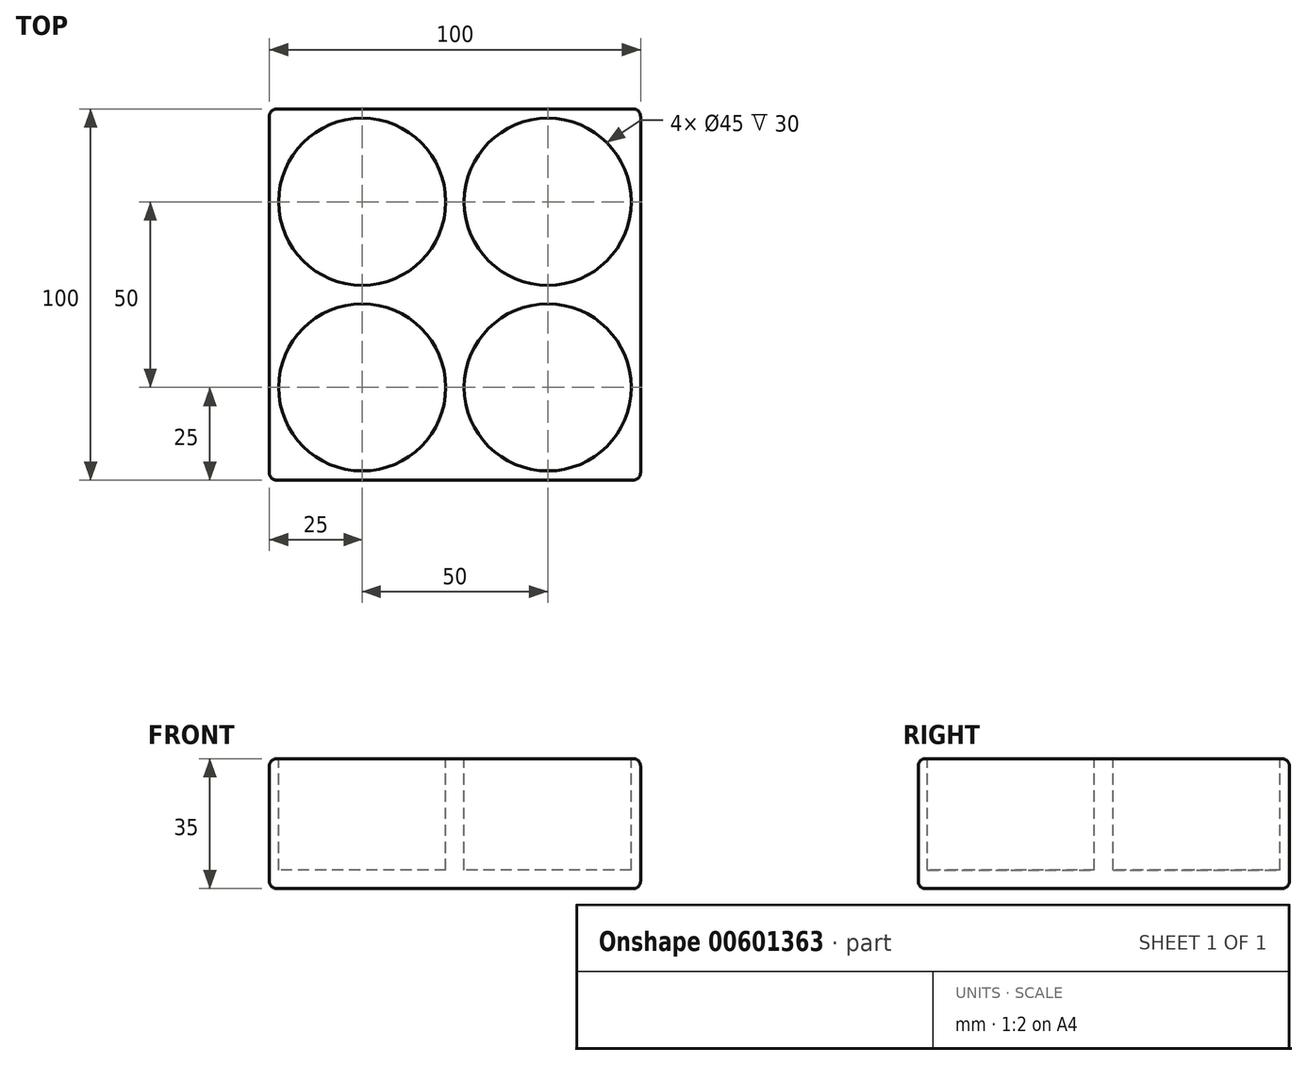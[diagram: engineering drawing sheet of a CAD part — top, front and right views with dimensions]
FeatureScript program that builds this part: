
annotation { "Feature Type Name" : "Feature", "Feature Type Description" : "" }
export const myFeature = defineFeature(function(context is Context, id is Id, definition is map)
    precondition{}
    {
        {
            var Q0;
            Q0=qCreatedBy(makeId("Top.planeOp"),FACE);
            var sketch = newSketch(context, id + "F0", { "sketchPlane" : qUnion([Q0])});
            skLineSegment(sketch, "E0.bottom", {"start": v(50, -50) * mm, "end": v(-50, -50) * mm});
            skLineSegment(sketch, "E0.top", {"start": v(50, 50) * mm, "end": v(-50, 50) * mm});
            skLineSegment(sketch, "E0.left", {"start": v(50, -50) * mm, "end": v(50, 50) * mm});
            skLineSegment(sketch, "E0.right", {"start": v(-50, -50) * mm, "end": v(-50, 50) * mm});
            skPoint(sketch, "E0.middle", {"position": v(0, 0) * mm});
            skPoint(sketch, "E1", {"position": v(-25, 25) * mm});
            skLineSegment(sketch, "E2", {"start": v(-50, 0) * mm, "end": v(50, 0) * mm});
            skLineSegment(sketch, "E3", {"start": v(0, 50) * mm, "end": v(0, 0) * mm});
            skLineSegment(sketch, "E4", {"start": v(-50, 50) * mm, "end": v(0, 0) * mm});
            skLineSegment(sketch, "E5", {"start": v(50, 50) * mm, "end": v(0, 0) * mm});
            skPoint(sketch, "E6", {"position": v(25, 25) * mm});
            skLineSegment(sketch, "E7", {"start": v(-50, -50) * mm, "end": v(0, 0) * mm});
            skPoint(sketch, "E8", {"position": v(-25, -25) * mm});
            skLineSegment(sketch, "E9", {"start": v(0, 0) * mm, "end": v(50, -50) * mm});
            skPoint(sketch, "E10", {"position": v(25, -25) * mm});
            skSolve(sketch);
        }
        {
            var Q0;
            Q0 = qSketchRegion(id + "F0", true);
            extrude(context, id + "F1", {"entities" : qUnion([Q0]), "depth" : 35 * mm, "offsetDistance" : 25 * mm});
        }
        {
            var Q0;
            Q0=makeQuery(id+"F1.opExtrude","CAP_FACE",FACE,{"disambiguationData":[OSD([sQuery(id+"F0.wireOp",EDGE,"E0.bottom"),sQuery(id+"F0.wireOp",EDGE,"E0.top"),sQuery(id+"F0.wireOp",EDGE,"E0.left"),sQuery(id+"F0.wireOp",EDGE,"E0.right")])],"isStart":false});
            var sketch = newSketch(context, id + "F2", { "sketchPlane" : qUnion([Q0])});
            skLineSegment(sketch, "E11", {"start": v(-50, 50) * mm, "end": v(0, 0) * mm});
            skPoint(sketch, "E12", {"position": v(-25, 25) * mm});
            skLineSegment(sketch, "E13", {"start": v(50, 50) * mm, "end": v(0, 0) * mm});
            skPoint(sketch, "E14", {"position": v(25, 25) * mm});
            skLineSegment(sketch, "E15", {"start": v(-50, -50) * mm, "end": v(0, 0) * mm});
            skPoint(sketch, "E16", {"position": v(-25, -25) * mm});
            skLineSegment(sketch, "E17", {"start": v(50, -50) * mm, "end": v(0, 0) * mm});
            skPoint(sketch, "E18", {"position": v(25, -25) * mm});
            skCircle(sketch, "E19", {"center": v(-25, 25) * mm, "radius": 22.5 * mm});
            skCircle(sketch, "E20", {"center": v(25, 25) * mm, "radius": 22.5 * mm});
            skCircle(sketch, "E21", {"center": v(-25, -25) * mm, "radius": 22.5 * mm});
            skCircle(sketch, "E22", {"center": v(25, -25) * mm, "radius": 22.5 * mm});
            skSolve(sketch);
        }
        {
            var Q0;
            {var subQ0=sQuery(id+"F2.wireOp",EDGE,"E19");var subQ1=sQuery(id+"F2.wireOp",EDGE,"E11");var subQ2=makeQuery(id+"F2.imprint","INTERSECT",VERTEX,{"disambiguationData":[OD(0.0)],"derivedFrom":[subQ1,subQ0]});Q0=makeQuery(id+"F2.imprint","IMPRINT",FACE,{"disambiguationData":[TD([[makeQuery(id+"F2.imprint","IMPRINT",EDGE,{"disambiguationData":[TD([[subQ2,-1.0]])],"derivedFrom":subQ1}),1.0]])]});}
            var Q1;
            {var subQ0=sQuery(id+"F2.wireOp",EDGE,"E19");var subQ1=sQuery(id+"F2.wireOp",EDGE,"E11");var subQ2=makeQuery(id+"F2.imprint","INTERSECT",VERTEX,{"disambiguationData":[OD(0.0)],"derivedFrom":[subQ1,subQ0]});Q1=makeQuery(id+"F2.imprint","IMPRINT",FACE,{"disambiguationData":[TD([[makeQuery(id+"F2.imprint","IMPRINT",EDGE,{"disambiguationData":[TD([[subQ2,-1.0]])],"derivedFrom":subQ1}),-1.0]])]});}
            var Q2;
            {var subQ0=sQuery(id+"F2.wireOp",EDGE,"E20");var subQ1=sQuery(id+"F2.wireOp",EDGE,"E13");var subQ2=makeQuery(id+"F2.imprint","INTERSECT",VERTEX,{"disambiguationData":[OD(0.0)],"derivedFrom":[subQ1,subQ0]});Q2=makeQuery(id+"F2.imprint","IMPRINT",FACE,{"disambiguationData":[TD([[makeQuery(id+"F2.imprint","IMPRINT",EDGE,{"disambiguationData":[TD([[subQ2,-1.0]])],"derivedFrom":subQ1}),-1.0]])]});}
            var Q3;
            {var subQ0=sQuery(id+"F2.wireOp",EDGE,"E20");var subQ1=sQuery(id+"F2.wireOp",EDGE,"E13");var subQ2=makeQuery(id+"F2.imprint","INTERSECT",VERTEX,{"disambiguationData":[OD(0.0)],"derivedFrom":[subQ1,subQ0]});Q3=makeQuery(id+"F2.imprint","IMPRINT",FACE,{"disambiguationData":[TD([[makeQuery(id+"F2.imprint","IMPRINT",EDGE,{"disambiguationData":[TD([[subQ2,-1.0]])],"derivedFrom":subQ1}),1.0]])]});}
            var Q4;
            {var subQ0=sQuery(id+"F2.wireOp",EDGE,"E22");var subQ1=sQuery(id+"F2.wireOp",EDGE,"E17");var subQ2=makeQuery(id+"F2.imprint","INTERSECT",VERTEX,{"disambiguationData":[OD(0.0)],"derivedFrom":[subQ1,subQ0]});Q4=makeQuery(id+"F2.imprint","IMPRINT",FACE,{"disambiguationData":[TD([[makeQuery(id+"F2.imprint","IMPRINT",EDGE,{"disambiguationData":[TD([[subQ2,-1.0]])],"derivedFrom":subQ1}),-1.0]])]});}
            var Q5;
            {var subQ0=sQuery(id+"F2.wireOp",EDGE,"E22");var subQ1=sQuery(id+"F2.wireOp",EDGE,"E17");var subQ2=makeQuery(id+"F2.imprint","INTERSECT",VERTEX,{"disambiguationData":[OD(0.0)],"derivedFrom":[subQ1,subQ0]});Q5=makeQuery(id+"F2.imprint","IMPRINT",FACE,{"disambiguationData":[TD([[makeQuery(id+"F2.imprint","IMPRINT",EDGE,{"disambiguationData":[TD([[subQ2,-1.0]])],"derivedFrom":subQ1}),1.0]])]});}
            var Q6;
            {var subQ0=sQuery(id+"F2.wireOp",EDGE,"E21");var subQ1=sQuery(id+"F2.wireOp",EDGE,"E15");var subQ2=makeQuery(id+"F2.imprint","INTERSECT",VERTEX,{"disambiguationData":[OD(0.0)],"derivedFrom":[subQ1,subQ0]});Q6=makeQuery(id+"F2.imprint","IMPRINT",FACE,{"disambiguationData":[TD([[makeQuery(id+"F2.imprint","IMPRINT",EDGE,{"disambiguationData":[TD([[subQ2,-1.0]])],"derivedFrom":subQ1}),-1.0]])]});}
            var Q7;
            {var subQ0=sQuery(id+"F2.wireOp",EDGE,"E21");var subQ1=sQuery(id+"F2.wireOp",EDGE,"E15");var subQ2=makeQuery(id+"F2.imprint","INTERSECT",VERTEX,{"disambiguationData":[OD(0.0)],"derivedFrom":[subQ1,subQ0]});Q7=makeQuery(id+"F2.imprint","IMPRINT",FACE,{"disambiguationData":[TD([[makeQuery(id+"F2.imprint","IMPRINT",EDGE,{"disambiguationData":[TD([[subQ2,-1.0]])],"derivedFrom":subQ1}),1.0]])]});}
            extrude(context, id + "F3", {"entities" : qUnion([Q0, Q1, Q2, Q3, Q4, Q5, Q6, Q7]), "operationType" : NewBodyOperationType.REMOVE, "oppositeDirection" : true, "depth" : 30 * mm, "offsetDistance" : 25 * mm});
        }
        {
            var Q0;
            Q0=makeQuery(id+"F1.opExtrude","SWEPT_EDGE",EDGE,{"disambiguationData":[OSD([sQuery(id+"F0.wireOp",EDGE,"E0.top"),sQuery(id+"F0.wireOp",EDGE,"E0.left"),sQuery(id+"F0.wireOp",EDGE,"E5")])]});
            var Q1;
            Q1=makeQuery(id+"F1.opExtrude","CAP_EDGE",EDGE,{"disambiguationData":[OSD([sQuery(id+"F0.wireOp",EDGE,"E0.top")])],"isStart":false});
            var Q2;
            Q2=makeQuery(id+"F1.opExtrude","SWEPT_EDGE",EDGE,{"disambiguationData":[OSD([sQuery(id+"F0.wireOp",EDGE,"E0.top"),sQuery(id+"F0.wireOp",EDGE,"E0.right"),sQuery(id+"F0.wireOp",EDGE,"E4")])]});
            var Q3;
            Q3=makeQuery(id+"F1.opExtrude","CAP_EDGE",EDGE,{"disambiguationData":[OSD([sQuery(id+"F0.wireOp",EDGE,"E0.top")])],"isStart":true});
            var Q4;
            Q4=makeQuery(id+"F1.opExtrude","CAP_EDGE",EDGE,{"disambiguationData":[OSD([sQuery(id+"F0.wireOp",EDGE,"E0.right")])],"isStart":false});
            var Q5;
            Q5=makeQuery(id+"F1.opExtrude","CAP_EDGE",EDGE,{"disambiguationData":[OSD([sQuery(id+"F0.wireOp",EDGE,"E0.left")])],"isStart":false});
            var Q6;
            Q6=makeQuery(id+"F1.opExtrude","CAP_EDGE",EDGE,{"disambiguationData":[OSD([sQuery(id+"F0.wireOp",EDGE,"E0.left")])],"isStart":true});
            var Q7;
            Q7=makeQuery(id+"F1.opExtrude","SWEPT_EDGE",EDGE,{"disambiguationData":[OSD([sQuery(id+"F0.wireOp",EDGE,"E0.bottom"),sQuery(id+"F0.wireOp",EDGE,"E0.left"),sQuery(id+"F0.wireOp",EDGE,"E9")])]});
            var Q8;
            Q8=makeQuery(id+"F1.opExtrude","CAP_EDGE",EDGE,{"disambiguationData":[OSD([sQuery(id+"F0.wireOp",EDGE,"E0.bottom")])],"isStart":false});
            var Q9;
            Q9=makeQuery(id+"F1.opExtrude","CAP_EDGE",EDGE,{"disambiguationData":[OSD([sQuery(id+"F0.wireOp",EDGE,"E0.bottom")])],"isStart":true});
            var Q10;
            Q10=makeQuery(id+"F1.opExtrude","SWEPT_EDGE",EDGE,{"disambiguationData":[OSD([sQuery(id+"F0.wireOp",EDGE,"E0.bottom"),sQuery(id+"F0.wireOp",EDGE,"E0.right"),sQuery(id+"F0.wireOp",EDGE,"E7")])]});
            var Q11;
            Q11=makeQuery(id+"F1.opExtrude","CAP_EDGE",EDGE,{"disambiguationData":[OSD([sQuery(id+"F0.wireOp",EDGE,"E0.right")])],"isStart":true});
            var Q12;
            Q12=makeQuery(id+"F3.boolean.opBoolean","COPY",EDGE,{"derivedFrom":makeQuery(id+"F3.opExtrude","CAP_EDGE",EDGE,{"disambiguationData":[OSD([sQuery(id+"F2.wireOp",EDGE,"E22")])],"isStart":true})});
            var Q13;
            Q13=makeQuery(id+"F3.boolean.opBoolean","COPY",EDGE,{"derivedFrom":makeQuery(id+"F3.opExtrude","CAP_EDGE",EDGE,{"disambiguationData":[OSD([sQuery(id+"F2.wireOp",EDGE,"E21")])],"isStart":true})});
            var Q14;
            Q14=makeQuery(id+"F3.boolean.opBoolean","COPY",EDGE,{"derivedFrom":makeQuery(id+"F3.opExtrude","CAP_EDGE",EDGE,{"disambiguationData":[OSD([sQuery(id+"F2.wireOp",EDGE,"E20")])],"isStart":true})});
            var Q15;
            Q15=makeQuery(id+"F3.boolean.opBoolean","COPY",EDGE,{"derivedFrom":makeQuery(id+"F3.opExtrude","CAP_EDGE",EDGE,{"disambiguationData":[OSD([sQuery(id+"F2.wireOp",EDGE,"E19")])],"isStart":true})});
            fillet(context, id + "F4", {"entities" : qUnion([Q0, Q1, Q2, Q3, Q4, Q5, Q6, Q7, Q8, Q9, Q10, Q11, Q12, Q13, Q14, Q15]), "radius" : 2 * mm, "tangentPropagation" : true, "allowEdgeOverflow" : false});
        }
    });
